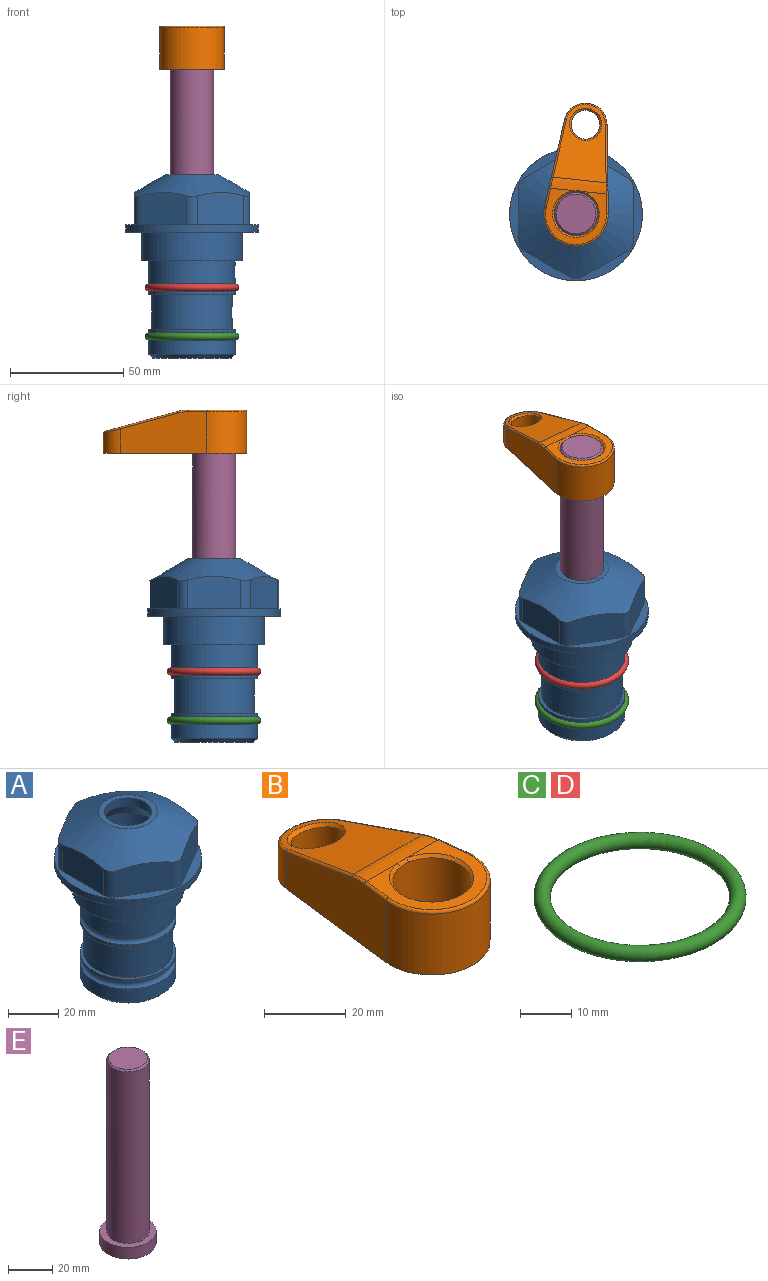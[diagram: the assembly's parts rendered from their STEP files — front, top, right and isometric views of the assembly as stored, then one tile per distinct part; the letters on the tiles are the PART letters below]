
ASSEMBLY  parts=5 mates=4
PART A: 36 faces, bbox 58.7x58.7x81 mm
  f0: cylinder r=17.78mm len=35.56mm, axis (0,0,1), area 1670.8mm2, adj f23,f24,f31
  f1: cylinder r=19.05mm len=38.1mm, axis (0,0,1), area 1191.9mm2, adj f26,f27,f30
  f2: plane 58.66x58.66mm, normal (0,0,-1), area 1150.6mm2, adj f3,f28
  f3: cylinder r=29.33mm len=58.66mm, axis (0,0,-1), area 585.1mm2, adj f2,f4
  f4: plane 58.66x58.66mm, normal (0,0,1), area 475.9mm2, adj f3,f5,f6,f7,f8,f9,f10,f11
  f5: plane 20.32x14.34mm, normal (-0.5,0.87,0), area 324.4mm2, adj f4,f15,f16,f17
  f6: plane 20.32x14.34mm, normal (0.5,0.87,0), area 324.4mm2, adj f4,f14,f15,f17
  f7: plane 23.48x14.34mm, normal (1,0,0), area 324.4mm2, adj f4,f13,f14,f17
  f8: plane 20.32x14.34mm, normal (0.5,-0.87,0), area 324.4mm2, adj f4,f12,f13,f17
  f9: plane 20.32x14.34mm, normal (-0.5,-0.87,0), area 324.4mm2, adj f4,f11,f12,f17
  f10: plane 23.48x14.34mm, normal (-1,0,0), area 324.4mm2, adj f4,f11,f16,f17
  f11: cylinder r=5.08mm len=12.85mm, axis (0,0,-1), area 67.2mm2, adj f4,f9,f10,f17
  f12: cylinder r=5.08mm len=12.85mm, axis (0,0,-1), area 67.2mm2, adj f4,f8,f9,f17
  f13: cylinder r=5.08mm len=12.85mm, axis (0,0,-1), area 67.2mm2, adj f4,f7,f8,f17
  f14: cylinder r=5.08mm len=12.85mm, axis (0,0,-1), area 67.2mm2, adj f4,f6,f7,f17
  f15: cylinder r=5.08mm len=12.85mm, axis (0,0,-1), area 67.2mm2, adj f4,f5,f6,f17
  f16: cylinder r=5.08mm len=12.85mm, axis (0,0,-1), area 67.2mm2, adj f4,f5,f10,f17
  f17: cone r=11.73mm half-angle=60deg, axis (0,0,-1), area 2071.8mm2, adj f5,f6,f7,f8,f9,f10,f11,f12
  f18: plane 23.46x23.46mm, normal (0,0,1), area 147.4mm2, adj f17,f35
  f19: plane 34.93x34.93mm, normal (0,0,-1), area 958mm2, adj f29
  f20: cylinder r=19.05mm len=38.1mm, axis (0,0,1), area 760.1mm2, adj f21,f29
  f21: torus R=19.05mm, axis (0,0,1), area 565.3mm2, adj f20,f22
  f22: cylinder r=19.05mm len=38.1mm, axis (0,0,1), area 190mm2, adj f21,f23
  f23: plane 38.1x38.1mm, normal (0,0,1), area 146.9mm2, adj f0,f22
  f24: plane 38.1x38.1mm, normal (0,0,-1), area 146.9mm2, adj f0,f25
  f25: cylinder r=19.05mm len=38.1mm, axis (0,0,1), area 190mm2, adj f24,f26
  f26: torus R=19.05mm, axis (0,0,1), area 565.3mm2, adj f1,f25
  f27: plane 44.45x44.45mm, normal (0,0,-1), area 411.7mm2, adj f1,f28
  f28: cylinder r=22.23mm len=44.45mm, axis (0,0,1), area 1773.5mm2, adj f2,f27
  f29: cone r=19.05mm half-angle=45deg, axis (0,0,1), area 257.5mm2, adj f19,f20
  f30: cylinder r=3.17mm len=6.75mm, axis (-1,0,0), area 128mm2, adj f1,f33
  f31: cylinder r=3.17mm len=6.35mm, axis (-1,0,0), area 102.5mm2, adj f0,f33
  f32: plane 25.4x25.4mm, normal (0,0,1), area 506.7mm2, adj f33
  f33: cylinder r=12.7mm len=66.42mm, axis (0,0,-1), area 5236.2mm2, adj f30,f31,f32,f34
  f34: cone r=9.53mm half-angle=30deg, axis (0,0,-1), area 443.4mm2, adj f33,f35
  f35: cylinder r=9.53mm len=19.05mm, axis (0,0,-1), area 240.9mm2, adj f18,f34
PART B: 31 faces, bbox 31.7x65.5x19.8 mm
  f0: plane 39.12x18.26mm, normal (0.99,0.12,0), area 612.2mm2, adj f1,f4,f7,f11,f13,f15
  f1: cylinder r=9.53mm len=18.91mm, axis (0,0,-1), area 296.1mm2, adj f0,f2,f7,f17
  f2: plane 39.12x18.26mm, normal (-0.99,0.12,0), area 612.2mm2, adj f1,f4,f7,f12,f14,f16
  f3: cylinder r=6.35mm len=12.7mm, axis (0,0,-1), area 362.4mm2, adj f7,f18
  f4: cylinder r=14.29mm len=28.58mm, axis (0,0,-1), area 882.2mm2, adj f0,f2,f7,f10
  f5: cylinder r=9.53mm len=19.05mm, axis (0,0,-1), area 1092.6mm2, adj f7,f19,f20
  f6: plane 26.99x23.69mm, normal (0,0,1), area 216.2mm2, adj f9,f10,f11,f12,f19
  f7: plane 63.5x28.58mm, normal (0,0,-1), area 661.8mm2, adj f0,f1,f2,f3,f4,f5,f22,f23
  f8: plane 33.52x23.6mm, normal (0,0.26,0.97), area 486mm2, adj f9,f15,f16,f17,f18
  f9: cylinder r=19.05mm len=24.72mm, axis (1,0,0), area 120.4mm2, adj f6,f8,f13,f14,f20
  f10: torus R=13.49mm, axis (0,0,1), area 59mm2, adj f4,f6,f11,f12
  f11: cylinder r=0.79mm len=8.67mm, axis (0.12,-0.99,0), area 10.8mm2, adj f0,f6,f10,f13
  f12: cylinder r=0.79mm len=8.67mm, axis (0.12,0.99,0), area 10.8mm2, adj f2,f6,f10,f14
  f13: bspline ~4.95x1.42mm, area 6.1mm2, adj f0,f9,f11,f15
  f14: bspline ~4.95x1.42mm, area 6.1mm2, adj f2,f9,f12,f16
  f15: cylinder r=0.79mm len=25.95mm, axis (0.12,-0.96,0.26), area 32.9mm2, adj f0,f8,f13,f17
  f16: cylinder r=0.79mm len=25.95mm, axis (0.12,0.96,-0.26), area 32.9mm2, adj f2,f8,f14,f17
  f17: bspline ~18.91x8.38mm, area 30mm2, adj f1,f8,f15,f16
  f18: bspline ~14.29x14.29mm, area 48.3mm2, adj f3,f8
  f19: cone r=9.53mm half-angle=45deg, axis (0,0,1), area 66.5mm2, adj f5,f6,f20
  f20: bspline ~3.22x0.96mm, area 3.5mm2, adj f5,f9,f19
  f21: plane 2.75x2.72mm, normal (0,0,-1), area 2.9mm2, adj f23,f25,f28
  f22: plane 23.05x15.88mm, normal (-0.99,-0.12,0), area 323.6mm2, adj f7,f25,f26,f27,f28,f29
  f23: plane 23.05x15.88mm, normal (0.99,-0.12,0), area 323.6mm2, adj f7,f21,f25,f27,f28,f30
  f24: cylinder r=9.53mm len=10.69mm, axis (0,0,-1), area 114.7mm2, adj f7,f27,f29,f30
  f25: cylinder r=12.7mm len=20.59mm, axis (0,0,-1), area 381.1mm2, adj f7,f21,f22,f23,f26,f28
  f26: plane 2.75x2.72mm, normal (0,0,-1), area 2.9mm2, adj f22,f25,f28
  f27: plane 19.72x18.37mm, normal (0,-0.26,-0.97), area 291.8mm2, adj f22,f23,f24,f28,f29,f30
  f28: cylinder r=15.88mm len=19.92mm, axis (1,0,0), area 54.8mm2, adj f21,f22,f23,f25,f26,f27
  f29: cylinder r=1.59mm len=11mm, axis (0,0,-1), area 34.7mm2, adj f7,f22,f24,f27
  f30: cylinder r=1.59mm len=11mm, axis (0,0,-1), area 34.7mm2, adj f7,f23,f24,f27
PART C: 1 faces, bbox 44.7x44.7x3.2 mm
  f0: torus R=19.05mm, axis (0,0,1), area 1193.9mm2
PART D: same geometry as C
PART E: 6 faces, bbox 25.4x25.4x101.6 mm
  f0: plane 17.46x17.46mm, normal (0,0,1), area 239.5mm2, adj f5
  f1: plane 25.4x25.4mm, normal (0,0,-1), area 506.7mm2, adj f2
  f2: cylinder r=12.7mm len=25.4mm, axis (0,0,1), area 506.7mm2, adj f1,f3
  f3: plane 25.4x25.4mm, normal (0,0,1), area 221.7mm2, adj f2,f4
  f4: cylinder r=9.53mm len=94.46mm, axis (0,0,1), area 5653mm2, adj f3,f5
  f5: cone r=8.73mm half-angle=45deg, axis (0,0,-1), area 64.4mm2, adj f0,f4
PLACE A at identity fixed
PLACE B rot(axis=(0,0,-1),6.1deg) t=(0,0,27.55)mm
PLACE C t=(0,0,-21.59)mm
PLACE D at identity
PLACE E rot(axis=(0,0,-1),6.1deg) t=(0,0,27.55)mm
MATE fastened D.f0 <-> A.f0  axis (0,0,1) through (0,0,-24.51)mm
MATE fastened E.f2 <-> B.f4  axis (0,0,1) through (0,0,91.05)mm
MATE fastened C.f0 <-> A.f0  axis (0,0,1) through (0,0,-46.1)mm
MATE cylindrical E.f2 <-> A.f0  axis (0,0,1) through (0,0,-10.55)mm
